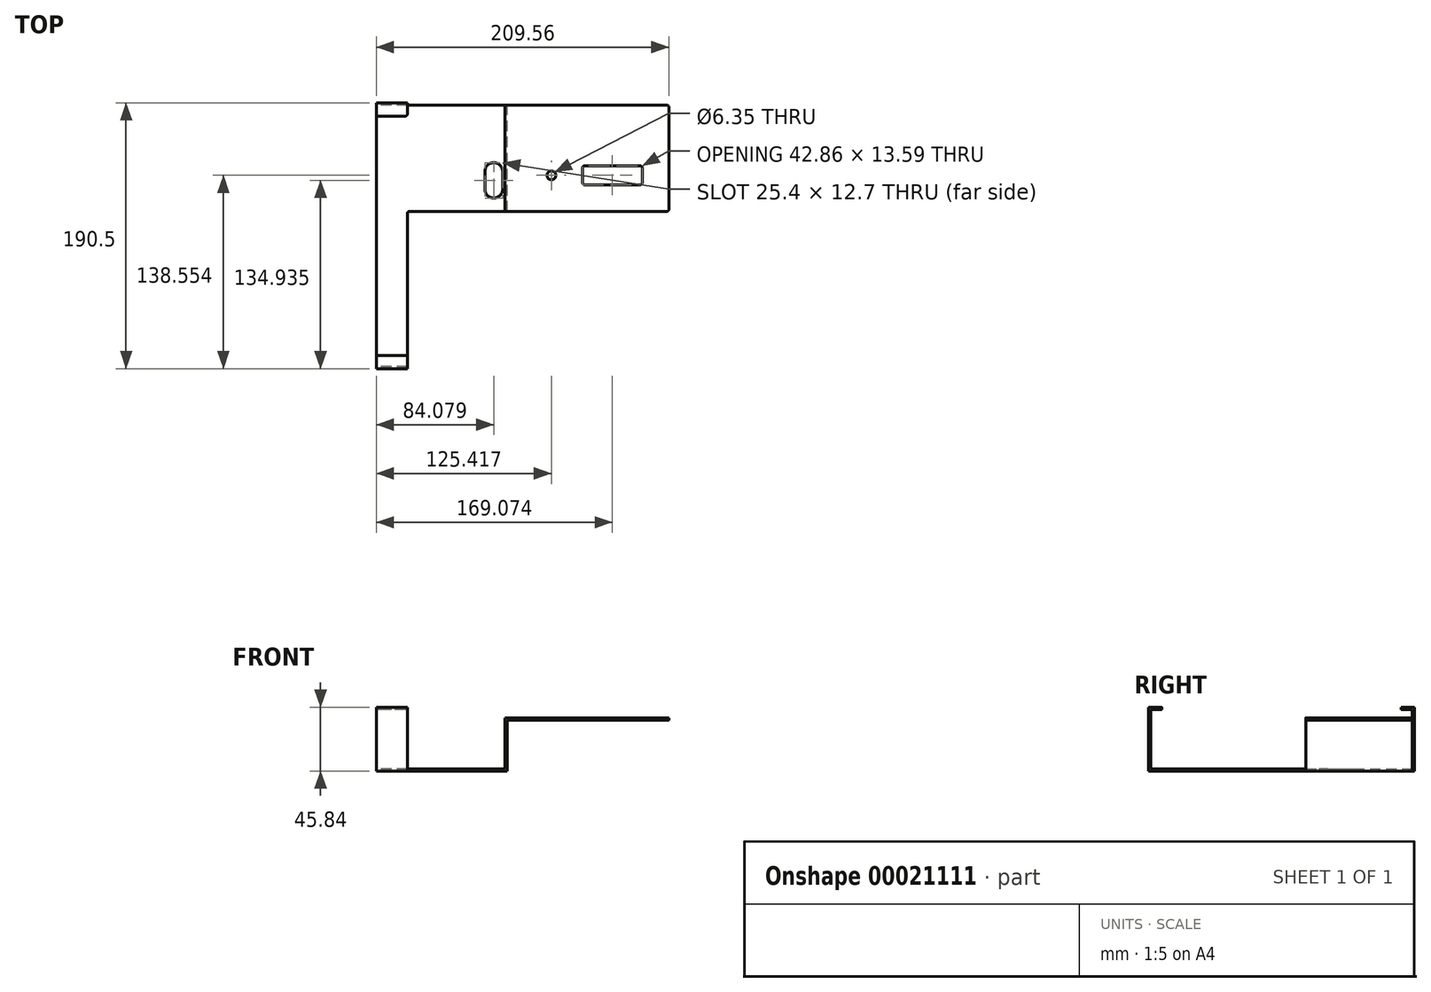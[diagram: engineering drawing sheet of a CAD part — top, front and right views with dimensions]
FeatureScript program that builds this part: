
annotation { "Feature Type Name" : "Feature", "Feature Type Description" : "" }
export const myFeature = defineFeature(function(context is Context, id is Id, definition is map)
    precondition{}
    {
        {
            var Q0;
            Q0=qCreatedBy(makeId("Front.planeOp"),FACE);
            var sketch = newSketch(context, id + "F0", { "sketchPlane" : qUnion([Q0])});
            skLineSegment(sketch, "E0", {"start": v(0, 0) * mm, "end": v(117.48, 0) * mm});
            skLineSegment(sketch, "E1", {"start": v(0, 0) * mm, "end": v(0, -36.58) * mm});
            skLineSegment(sketch, "E2", {"start": v(0, -36.58) * mm, "end": v(-92.08, -36.58) * mm});
            skLineSegment(sketch, "E3.0", {"start": v(0, -1.59) * mm, "end": v(117.48, -1.59) * mm});
            skLineSegment(sketch, "E4.0", {"start": v(0, -38.16) * mm, "end": v(-92.08, -38.16) * mm});
            skLineSegment(sketch, "E5.0", {"start": v(1.59, -38.16) * mm, "end": v(-92.08, -38.16) * mm});
            skLineSegment(sketch, "E5.1", {"start": v(1.59, -1.59) * mm, "end": v(1.59, -38.16) * mm});
            skLineSegment(sketch, "E5.2", {"start": v(1.59, -1.59) * mm, "end": v(117.48, -1.59) * mm});
            skLineSegment(sketch, "E6", {"start": v(117.48, 0) * mm, "end": v(117.48, -1.59) * mm});
            skLineSegment(sketch, "E7", {"start": v(-92.08, -38.16) * mm, "end": v(-92.08, -36.58) * mm});
            skSolve(sketch);
        }
        {
            var Q0;
            Q0 = qSketchRegion(id + "F0", true);
            extrude(context, id + "F1", {"entities" : qUnion([Q0]), "endBound" : BoundingType.SYMMETRIC, "depth" : 76.2 * mm});
        }
        {
            var Q0;
            Q0=makeQuery(id+"F1.opExtrude","SWEPT_FACE",FACE,{"disambiguationData":[OSD([sQuery(id+"F0.wireOp",EDGE,"E7")])]});
            var sketch = newSketch(context, id + "F2", { "sketchPlane" : qUnion([Q0])});
            skLineSegment(sketch, "E8", {"start": v(-38.1, -36.58) * mm, "end": v(-38.1, 6.1) * mm});
            skLineSegment(sketch, "E9", {"start": v(-38.1, 6.1) * mm, "end": v(-30.16, 6.1) * mm});
            skLineSegment(sketch, "E10.0", {"start": v(-39.69, -36.58) * mm, "end": v(-39.69, 7.68) * mm});
            skLineSegment(sketch, "E11.0", {"start": v(-39.69, 7.68) * mm, "end": v(-30.16, 7.68) * mm});
            skLineSegment(sketch, "E12", {"start": v(-30.16, 7.68) * mm, "end": v(-30.16, 6.1) * mm});
            skLineSegment(sketch, "E13", {"start": v(-39.69, -36.58) * mm, "end": v(-39.69, -38.16) * mm});
            skLineSegment(sketch, "E14", {"start": v(-39.69, -38.16) * mm, "end": v(-38.1, -38.16) * mm});
            skLineSegment(sketch, "E15", {"start": v(-38.1, -38.16) * mm, "end": v(-38.1, -36.58) * mm});
            skLineSegment(sketch, "E16.0", {"start": v(38.1, -38.16) * mm, "end": v(-38.1, -38.16) * mm});
            skLineSegment(sketch, "E17.0.0", {"start": v(-38.1, -36.58) * mm, "end": v(-38.1, -38.16) * mm});
            skLineSegment(sketch, "E17.0.1", {"start": v(-38.1, -38.16) * mm, "end": v(150.81, -38.16) * mm});
            skLineSegment(sketch, "E17.0.2", {"start": v(38.1, -38.16) * mm, "end": v(38.1, -36.58) * mm});
            skLineSegment(sketch, "E17.0.3", {"start": v(149.22, -36.58) * mm, "end": v(-38.1, -36.58) * mm});
            skLineSegment(sketch, "E18.0", {"start": v(149.23, -38.16) * mm, "end": v(149.23, 6.1) * mm});
            skLineSegment(sketch, "E19", {"start": v(149.23, 6.1) * mm, "end": v(141.29, 6.1) * mm});
            skLineSegment(sketch, "E20", {"start": v(-33.6, 7.68) * mm, "end": v(163.44, 7.68) * mm, "construction": true});
            skLineSegment(sketch, "E21.0", {"start": v(150.81, -38.16) * mm, "end": v(150.81, 7.68) * mm});
            skLineSegment(sketch, "E22.0", {"start": v(149.23, 7.68) * mm, "end": v(141.29, 7.68) * mm});
            skLineSegment(sketch, "E23", {"start": v(141.29, 6.1) * mm, "end": v(141.29, 7.68) * mm});
            skLineSegment(sketch, "E24", {"start": v(149.23, 7.68) * mm, "end": v(150.81, 7.68) * mm});
            skSolve(sketch);
        }
        {
            var Q0;
            Q0 = qSketchRegion(id + "F2", true);
            extrude(context, id + "F3", {"entities" : qUnion([Q0]), "operationType" : NewBodyOperationType.ADD, "oppositeDirection" : true, "depth" : 22.22 * mm});
        }
        {
            var Q0;
            Q0=makeQuery(id+"F3.boolean.opBoolean","MERGE",FACE,{"derivedFrom":[makeQuery(id+"F1.opExtrude","SWEPT_FACE",FACE,{"disambiguationData":[OSD([sQuery(id+"F0.wireOp",EDGE,"E5.0")])]}),makeQuery(id+"F3.opExtrude","SWEPT_FACE",FACE,{"disambiguationData":[OSD([sQuery(id+"F2.wireOp",EDGE,"E14"),sQuery(id+"F2.wireOp",EDGE,"E17.0.1")])]})]});
            var sketch = newSketch(context, id + "F4", { "sketchPlane" : qUnion([Q0])});
            skLineSegment(sketch, "E25.0", {"start": v(1.59, 38.1) * mm, "end": v(-69.85, 38.1) * mm, "construction": true});
            skLineSegment(sketch, "E26.0", {"start": v(-92.08, 150.81) * mm, "end": v(-92.08, -39.69) * mm, "construction": true});
            skLineSegment(sketch, "E27.0", {"start": v(1.59, 28.58) * mm, "end": v(-69.85, 28.58) * mm, "construction": true});
            skLineSegment(sketch, "E28.0", {"start": v(-14.35, 150.81) * mm, "end": v(-14.35, -39.69) * mm, "construction": true});
            skLineSegment(sketch, "E29.0", {"start": v(-1.65, 150.81) * mm, "end": v(-1.65, -39.69) * mm, "construction": true});
            skLineSegment(sketch, "E30.0", {"start": v(1.59, 3.18) * mm, "end": v(-69.85, 3.18) * mm, "construction": true});
            skLineSegment(sketch, "E31.0", {"start": v(1.59, 9.53) * mm, "end": v(-69.85, 9.53) * mm, "construction": true});
            skLineSegment(sketch, "E32.0", {"start": v(-8, 150.81) * mm, "end": v(-8, -39.69) * mm, "construction": true});
            skLineSegment(sketch, "E33.0", {"start": v(1.59, 15.88) * mm, "end": v(-69.85, 15.88) * mm, "construction": true});
            skArc(sketch, "E34", {"start": v(-14.35, 9.52) * mm, "mid": v(-8, 3.17) * mm, "end": v(-1.65, 9.52) * mm});
            skArc(sketch, "E35.MirrorC", {"start": v(-14.35, 22.23) * mm, "mid": v(-8, 28.58) * mm, "end": v(-1.65, 22.23) * mm});
            skLineSegment(sketch, "E36", {"start": v(-14.35, 22.23) * mm, "end": v(-14.35, 9.52) * mm});
            skLineSegment(sketch, "E37", {"start": v(-14.35, 9.52) * mm, "end": v(-1.65, 9.52) * mm});
            skLineSegment(sketch, "E38", {"start": v(-1.65, 9.52) * mm, "end": v(-1.65, 22.23) * mm});
            skSolve(sketch);
        }
        {
            var Q0;
            Q0 = qSketchRegion(id + "F4", true);
            extrude(context, id + "F5", {"entities" : qUnion([Q0]), "operationType" : NewBodyOperationType.REMOVE, "endBound" : BoundingType.THROUGH_ALL, "oppositeDirection" : true, "depth" : 25.4 * mm});
        }
        {
            var Q0;
            Q0=makeQuery(id+"F1.opExtrude","SWEPT_FACE",FACE,{"disambiguationData":[OSD([sQuery(id+"F0.wireOp",EDGE,"E0")])]});
            var sketch = newSketch(context, id + "F6", { "sketchPlane" : qUnion([Q0])});
            skLineSegment(sketch, "E39.0", {"start": v(98.43, -38.1) * mm, "end": v(98.43, 38.1) * mm, "construction": true});
            skLineSegment(sketch, "E40.0", {"start": v(55.56, -38.1) * mm, "end": v(55.56, 38.1) * mm, "construction": true});
            skLineSegment(sketch, "E41.0", {"start": v(0, -19.05) * mm, "end": v(117.48, -19.05) * mm, "construction": true});
            skLineSegment(sketch, "E42.0", {"start": v(0, -5.46) * mm, "end": v(117.48, -5.46) * mm, "construction": true});
            skLineSegment(sketch, "E43.bottom", {"start": v(98.43, -19.05) * mm, "end": v(55.56, -19.05) * mm});
            skLineSegment(sketch, "E43.top", {"start": v(98.43, -5.46) * mm, "end": v(55.56, -5.46) * mm});
            skLineSegment(sketch, "E43.left", {"start": v(98.43, -19.05) * mm, "end": v(98.43, -5.46) * mm});
            skLineSegment(sketch, "E43.right", {"start": v(55.56, -19.05) * mm, "end": v(55.56, -5.46) * mm});
            skLineSegment(sketch, "E44", {"start": v(98.43, -12.26) * mm, "end": v(26.18, -12.26) * mm, "construction": true});
            skLineSegment(sketch, "E45.0", {"start": v(33.34, -38.1) * mm, "end": v(33.34, 38.1) * mm, "construction": true});
            skCircle(sketch, "E46", {"center": v(33.34, -12.26) * mm, "radius": 3.18 * mm});
            skSolve(sketch);
        }
        {
            var Q0;
            Q0 = qSketchRegion(id + "F6", true);
            extrude(context, id + "F7", {"entities" : qUnion([Q0]), "operationType" : NewBodyOperationType.REMOVE, "endBound" : BoundingType.THROUGH_ALL, "oppositeDirection" : true, "depth" : 25.4 * mm});
        }
        {
            var Q0;
            Q0=makeQuery(id+"F7.boolean.opBoolean","COPY",EDGE,{"derivedFrom":makeQuery(id+"F7.opExtrude","SWEPT_EDGE",EDGE,{"disambiguationData":[OSD([sQuery(id+"F6.wireOp",EDGE,"E43.top"),sQuery(id+"F6.wireOp",EDGE,"E43.right")])]})});
            var Q1;
            Q1=makeQuery(id+"F7.boolean.opBoolean","COPY",EDGE,{"derivedFrom":makeQuery(id+"F7.opExtrude","SWEPT_EDGE",EDGE,{"disambiguationData":[OSD([sQuery(id+"F6.wireOp",EDGE,"E43.bottom"),sQuery(id+"F6.wireOp",EDGE,"E43.right")])]})});
            var Q2;
            Q2=makeQuery(id+"F7.boolean.opBoolean","COPY",EDGE,{"derivedFrom":makeQuery(id+"F7.opExtrude","SWEPT_EDGE",EDGE,{"disambiguationData":[OSD([sQuery(id+"F6.wireOp",EDGE,"E43.top"),sQuery(id+"F6.wireOp",EDGE,"E43.left")])]})});
            var Q3;
            Q3=makeQuery(id+"F7.boolean.opBoolean","COPY",EDGE,{"derivedFrom":makeQuery(id+"F7.opExtrude","SWEPT_EDGE",EDGE,{"disambiguationData":[OSD([sQuery(id+"F6.wireOp",EDGE,"E43.bottom"),sQuery(id+"F6.wireOp",EDGE,"E43.left")])]})});
            fillet(context, id + "F8", {"entities" : qUnion([Q0, Q1, Q2, Q3]), "radius" : 1.59 * mm, "tangentPropagation" : true, "allowEdgeOverflow" : false});
        }
        {
            var Q0;
            Q0=makeQuery(id+"F1.opExtrude","CAP_EDGE",EDGE,{"disambiguationData":[OSD([sQuery(id+"F0.wireOp",EDGE,"E6")])],"isStart":false});
            var Q1;
            Q1=makeQuery(id+"F1.opExtrude","CAP_EDGE",EDGE,{"disambiguationData":[OSD([sQuery(id+"F0.wireOp",EDGE,"E6")])],"isStart":true});
            var Q2;
            Q2=makeQuery(id+"F3.opExtrude","CAP_EDGE",EDGE,{"disambiguationData":[OSD([sQuery(id+"F2.wireOp",EDGE,"E12")])],"isStart":false});
            var Q3;
            Q3=makeQuery(id+"F3.opExtrude","CAP_EDGE",EDGE,{"disambiguationData":[OSD([sQuery(id+"F2.wireOp",EDGE,"E12")])],"isStart":true});
            var Q4;
            Q4=makeQuery(id+"F3.opExtrude","CAP_EDGE",EDGE,{"disambiguationData":[OSD([sQuery(id+"F2.wireOp",EDGE,"E23")])],"isStart":false});
            var Q5;
            Q5=makeQuery(id+"F3.opExtrude","CAP_EDGE",EDGE,{"disambiguationData":[OSD([sQuery(id+"F2.wireOp",EDGE,"E23")])],"isStart":true});
            fillet(context, id + "F9", {"entities" : qUnion([Q0, Q1, Q2, Q3, Q4, Q5]), "radius" : 1.59 * mm, "tangentPropagation" : true, "allowEdgeOverflow" : false});
        }
        {
            var Q0;
            Q0=makeQuery(id+"F3.boolean.opBoolean","INTERSECT",EDGE,{"derivedFrom":[makeQuery(id+"F1.opExtrude","CAP_FACE",FACE,{"disambiguationData":[OSD([sQuery(id+"F0.wireOp",EDGE,"E0"),sQuery(id+"F0.wireOp",EDGE,"E1"),sQuery(id+"F0.wireOp",EDGE,"E2"),sQuery(id+"F0.wireOp",EDGE,"E5.0"),sQuery(id+"F0.wireOp",EDGE,"E5.1"),sQuery(id+"F0.wireOp",EDGE,"E5.2"),sQuery(id+"F0.wireOp",EDGE,"E6"),sQuery(id+"F0.wireOp",EDGE,"E7")])],"isStart":false}),makeQuery(id+"F3.opExtrude","CAP_FACE",FACE,{"disambiguationData":[OSD([sQuery(id+"F2.wireOp",EDGE,"E8"),sQuery(id+"F2.wireOp",EDGE,"E9"),sQuery(id+"F2.wireOp",EDGE,"E10.0"),sQuery(id+"F2.wireOp",EDGE,"E11.0"),sQuery(id+"F2.wireOp",EDGE,"E12"),sQuery(id+"F2.wireOp",EDGE,"E13"),sQuery(id+"F2.wireOp",EDGE,"E14"),sQuery(id+"F2.wireOp",EDGE,"E17.0.1"),sQuery(id+"F2.wireOp",EDGE,"E17.0.3"),sQuery(id+"F2.wireOp",EDGE,"E18.0"),sQuery(id+"F2.wireOp",EDGE,"E19"),sQuery(id+"F2.wireOp",EDGE,"E21.0"),sQuery(id+"F2.wireOp",EDGE,"E22.0"),sQuery(id+"F2.wireOp",EDGE,"E23"),sQuery(id+"F2.wireOp",EDGE,"E24")])],"isStart":false})]});
            fillet(context, id + "F10", {"entities" : qUnion([Q0]), "radius" : 1.59 * mm, "tangentPropagation" : true, "allowEdgeOverflow" : false});
        }
    });
